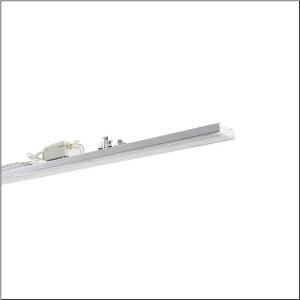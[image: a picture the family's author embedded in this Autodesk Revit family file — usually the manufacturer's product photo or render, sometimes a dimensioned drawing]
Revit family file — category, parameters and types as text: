
# Revit family: licross_11_recessed_mo_51te1edn495g
name_source: partatom
category: Lighting Fixtures
units: mm (PartAtom-declared; Revit-internal decimal feet)

## family parameters
Cut with Voids When Loaded = No
Host = Face
Light Source = No
Part Type = Normal
Room Calculation Point = No
Round Connector Dimension = Use Diameter
Shared = No

## types (1)
- --- (1 x LED, 9900 lm, 56.7 W, 4000K)
    Apparent Load = 57 VA
    CIE Flux Codes = 85 95 99 100 100
    Color Rendering = 80
    Color Temperature = 4000K
    Default Elevation = 1800 mm
    Description = Licross 11 Recessed MO, luminaire insert, of sheet steel, galvanised, coil coated, white, length: 1.500mm, width: 66mm, height: 67mm, LED rated luminous flux: 9.900lm, light colour: 840, SDCM (Standard Deviation of Colour Matching)MacAdam ≤ 2 SDCM (initial), control gear: DALI 2, with plug, 5-pole, with phase selection, mains connection: 220..240V, AC, 50/60Hz, rated input power: 57W, internal wiring halogen-free, primary light control with lens, of plastic, primary optical cover: cover, of PMMA, light emission: direct distribution, primary light characteristic: symmetric, protection rating (complete): IP54, insulation class (complete): insulation class I (protective earthing), certification: CE, ENEC, VDE, UKCA, protection symbol: D if used in an environment with non-conductive dust loads with corresponding accessories, impact resistance: IK06, permissible ambient temperature for indoor applications: -25..+35°C, corresponds to IFS (International Featured Standards) requirements for safety and quality in the food industry, reducing of maximum allowable ambient temperature of 5°C with ceiling mounting, LABS conformity tested according to VDMA 24364:2018-05, The light source and the operating device comply with the requirements of the Ecodesign Regulation (EU) 2019/2020 and are replaceable in accordance with this regulation, packaging unit: 1 piece
    Height = 58 mm
    Lamp = 1 x LED
    Lamp Light Flux = 9900 lm
    Lamp Power = 56.7 W
    Lamp count = 1
    Length = 1500 mm
    Luminous efficacy = 175 lm/W
    Manufacturer = Siteco
    ModVariant = No
    Model = 51TE1EDN495G
    Mounting Place = Ceiling
    Mounting Type = Pendant
    Number of Poles = 1
    OnlyDefault = Yes
    Power Factor = 1
    Product Name = Licross 11 Recessed MO
    Product group = luminaire insert | ceiling pendant
    ProductGroupID = 901
    Protection Class = Protection class I
    Protection Degree = IP 54
    RLX_Detail_Level = 1
    RLX_Emergency_Light_Flux = 0 lm
    RLX_Emergency_Type = 0
    RLX_Emergency_Type_DB = No
    RlxData = <blob elided: 24861 chars, md5=6cb01d7c>
    Socket = socket
    Standby Power = 0 W
    System Light Flux = 9900 lm
    System Power = 57 W
    Type Comments = factory setting: luminous flux: 100 % | dim-lin: 254 | 378 mA
    Type Image = l_1296930.jpg
    URL = http://relux.com
    VarID = @adj_101327
    Voltage = 0 V
    Weight = 0.00 kg
    Width = 66 mm

## geometry (parser evidence)
native form markers: Blend x4, Sweep x11
no freeform markers — native parametric forms only
